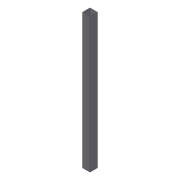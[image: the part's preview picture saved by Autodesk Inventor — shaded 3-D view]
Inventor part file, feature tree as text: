
AUTODESK INVENTOR PART (.ipt)
format: ipt  version: 2012 (Build 160160000, 160)  size: 71,168 bytes
history: native  units: in
note: dims shown in document units (in); Inventor stores cm internally (conversion verified against a paired STEP export)
features: extrude x1, shell x1, sketch x1
ambient origin geometry x8: Origin, YZ Plane, XZ Plane, XY Plane, X Axis, Y Axis, Z Axis, Center Point
bodies: Solid1 (feature_tree)
feature tree (3):
  extrude  "Extrusion1"  Depth=1.0in
  shell  "Shell1"  Thickness=1.0in
  sketch  "Sketch1"  dims[d0=18.0in d1=1.0in d2=1.0in d3=0.0in d4=0.0625in]
